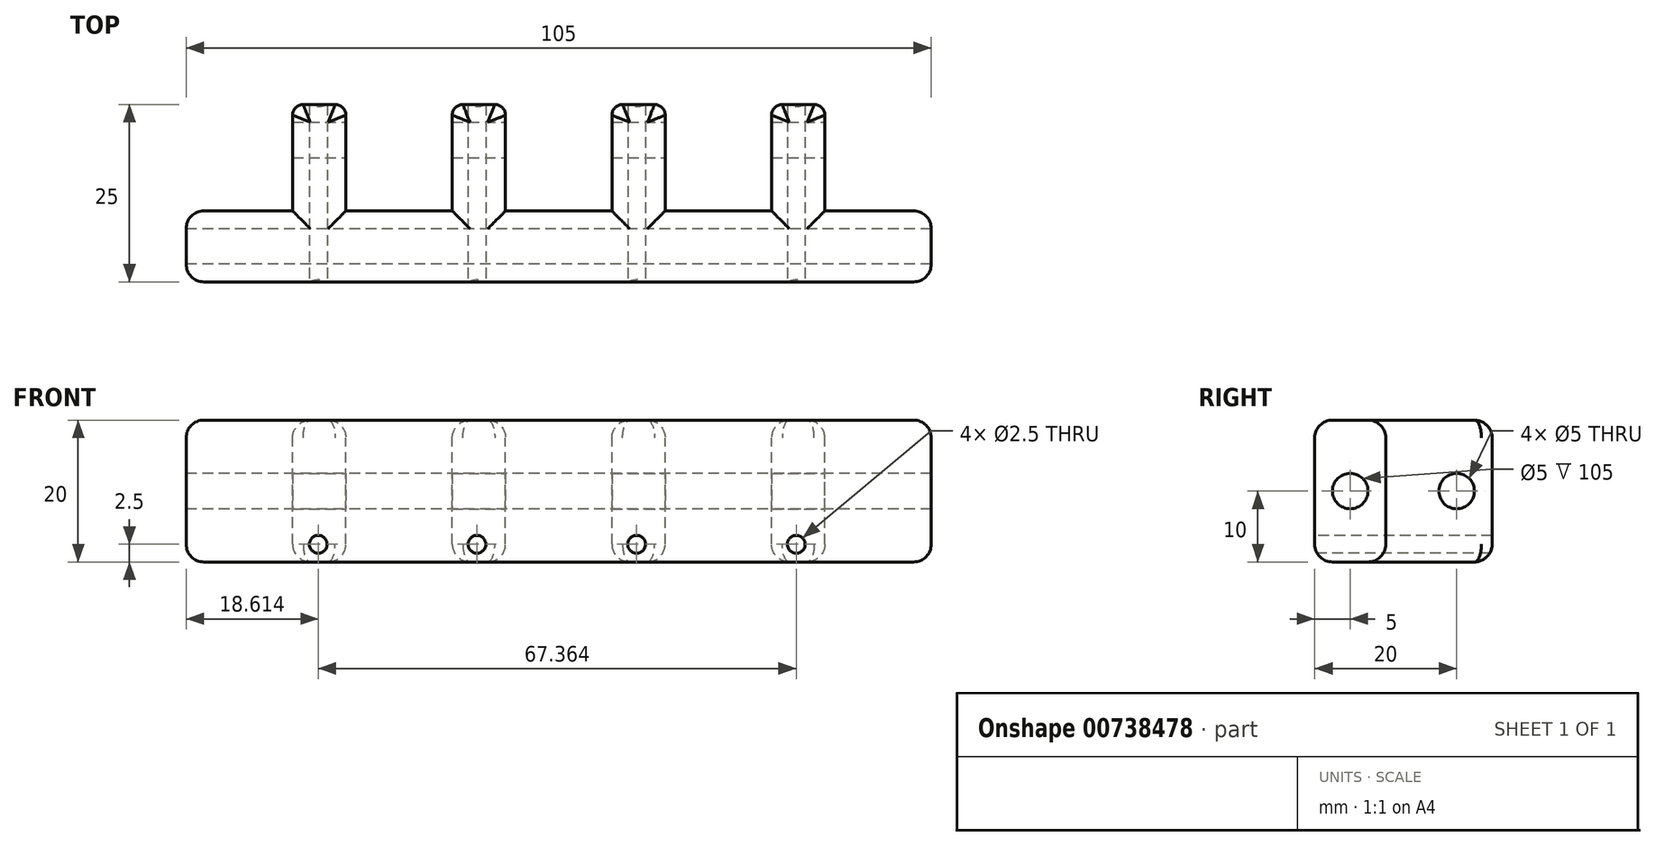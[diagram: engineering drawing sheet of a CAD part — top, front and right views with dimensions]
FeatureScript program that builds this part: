
annotation { "Feature Type Name" : "Feature", "Feature Type Description" : "" }
export const myFeature = defineFeature(function(context is Context, id is Id, definition is map)
    precondition{}
    {
        {
            var Q0;
            Q0=qCreatedBy(makeId("Top.planeOp"),FACE);
            var sketch = newSketch(context, id + "F0", { "sketchPlane" : qUnion([Q0])});
            skLineSegment(sketch, "E0.bottom", {"start": v(0, 0) * mm, "end": v(105, 0) * mm});
            skLineSegment(sketch, "E0.top", {"start": v(0, -25) * mm, "end": v(105, -25) * mm});
            skLineSegment(sketch, "E0.left", {"start": v(0, 0) * mm, "end": v(0, -25) * mm});
            skLineSegment(sketch, "E0.right", {"start": v(105, 0) * mm, "end": v(105, -25) * mm});
            skSolve(sketch);
        }
        {
            var Q0;
            Q0=makeQuery(id+"F0.imprint","IMPRINT",FACE,{"disambiguationData":[TD([[makeQuery(id+"F0.imprint","IMPRINT",EDGE,{"derivedFrom":sQuery(id+"F0.wireOp",EDGE,"E0.bottom")}),-1.0]])]});
            extrude(context, id + "F1", {"entities" : qUnion([Q0]), "depth" : 20 * mm, "offsetDistance" : 25 * mm});
        }
        {
            var Q0;
            Q0=makeQuery(id+"F1.opExtrude","CAP_FACE",FACE,{"disambiguationData":[OSD([sQuery(id+"F0.wireOp",EDGE,"E0.bottom"),sQuery(id+"F0.wireOp",EDGE,"E0.top"),sQuery(id+"F0.wireOp",EDGE,"E0.left"),sQuery(id+"F0.wireOp",EDGE,"E0.right")])],"isStart":false});
            var sketch = newSketch(context, id + "F2", { "sketchPlane" : qUnion([Q0])});
            skLineSegment(sketch, "E1", {"start": v(51.25, -10) * mm, "end": v(43.75, -10) * mm});
            skLineSegment(sketch, "E2", {"start": v(105, -15) * mm, "end": v(0, -15) * mm});
            skLineSegment(sketch, "E3", {"start": v(0, 0) * mm, "end": v(15, 0) * mm});
            skLineSegment(sketch, "E4", {"start": v(15, 0) * mm, "end": v(22.5, 0) * mm});
            skLineSegment(sketch, "E5", {"start": v(22.5, 0) * mm, "end": v(37.5, 0) * mm});
            skLineSegment(sketch, "E6", {"start": v(37.5, 0) * mm, "end": v(45, 0) * mm});
            skLineSegment(sketch, "E7", {"start": v(45, 0) * mm, "end": v(60, 0) * mm});
            skLineSegment(sketch, "E8", {"start": v(60, 0) * mm, "end": v(67.5, 0) * mm});
            skLineSegment(sketch, "E9", {"start": v(67.5, 0) * mm, "end": v(82.5, 0) * mm});
            skLineSegment(sketch, "E10", {"start": v(82.5, 0) * mm, "end": v(90, 0) * mm});
            skLineSegment(sketch, "E11", {"start": v(90, 0) * mm, "end": v(105, 0) * mm});
            skLineSegment(sketch, "E12.top", {"start": v(0, -15) * mm, "end": v(15, -15) * mm});
            skLineSegment(sketch, "E12.left", {"start": v(0, 0) * mm, "end": v(0, -15) * mm});
            skLineSegment(sketch, "E12.right", {"start": v(15, 0) * mm, "end": v(15, -15) * mm});
            skLineSegment(sketch, "E13.top", {"start": v(22.5, -15) * mm, "end": v(37.5, -15) * mm});
            skLineSegment(sketch, "E13.left", {"start": v(22.5, 0) * mm, "end": v(22.5, -15) * mm});
            skLineSegment(sketch, "E13.right", {"start": v(37.5, 0) * mm, "end": v(37.5, -15) * mm});
            skLineSegment(sketch, "E14.left", {"start": v(45, 0) * mm, "end": v(45, 0) * mm});
            skLineSegment(sketch, "E14.right", {"start": v(60, 0) * mm, "end": v(60, 0) * mm});
            skLineSegment(sketch, "E15.top", {"start": v(45, -15) * mm, "end": v(60, -15) * mm});
            skLineSegment(sketch, "E15.left", {"start": v(45, 0) * mm, "end": v(45, -15) * mm});
            skLineSegment(sketch, "E15.right", {"start": v(60, 0) * mm, "end": v(60, -15) * mm});
            skLineSegment(sketch, "E16.left", {"start": v(67.5, 0) * mm, "end": v(67.5, 0) * mm});
            skLineSegment(sketch, "E16.right", {"start": v(82.5, 0) * mm, "end": v(82.5, 0) * mm});
            skLineSegment(sketch, "E17.top", {"start": v(67.5, -15) * mm, "end": v(82.5, -15) * mm});
            skLineSegment(sketch, "E17.left", {"start": v(67.5, 0) * mm, "end": v(67.5, -15) * mm});
            skLineSegment(sketch, "E17.right", {"start": v(82.5, 0) * mm, "end": v(82.5, -15) * mm});
            skLineSegment(sketch, "E18.top", {"start": v(90, -15) * mm, "end": v(105, -15) * mm});
            skLineSegment(sketch, "E18.left", {"start": v(90, 0) * mm, "end": v(90, -15) * mm});
            skLineSegment(sketch, "E18.right", {"start": v(105, 0) * mm, "end": v(105, -15) * mm});
            skSolve(sketch);
        }
        {
            var Q0;
            Q0=makeQuery(id+"F2.imprint","IMPRINT",FACE,{"disambiguationData":[TD([[makeQuery(id+"F2.imprint","IMPRINT",EDGE,{"derivedFrom":sQuery(id+"F2.wireOp",EDGE,"E3")}),-1.0]])]});
            var Q1;
            Q1=makeQuery(id+"F2.imprint","IMPRINT",FACE,{"disambiguationData":[TD([[makeQuery(id+"F2.imprint","IMPRINT",EDGE,{"derivedFrom":sQuery(id+"F2.wireOp",EDGE,"E5")}),-1.0]])]});
            var Q2;
            Q2=makeQuery(id+"F2.imprint","IMPRINT",FACE,{"disambiguationData":[TD([[makeQuery(id+"F2.imprint","IMPRINT",EDGE,{"derivedFrom":sQuery(id+"F2.wireOp",EDGE,"E7")}),-1.0]])]});
            var Q3;
            Q3=makeQuery(id+"F2.imprint","IMPRINT",FACE,{"disambiguationData":[TD([[makeQuery(id+"F2.imprint","IMPRINT",EDGE,{"derivedFrom":sQuery(id+"F2.wireOp",EDGE,"E9")}),-1.0]])]});
            var Q4;
            Q4=makeQuery(id+"F2.imprint","IMPRINT",FACE,{"disambiguationData":[TD([[makeQuery(id+"F2.imprint","IMPRINT",EDGE,{"derivedFrom":sQuery(id+"F2.wireOp",EDGE,"E11")}),-1.0]])]});
            extrude(context, id + "F3", {"entities" : qUnion([Q0, Q1, Q2, Q3, Q4]), "operationType" : NewBodyOperationType.REMOVE, "endBound" : BoundingType.THROUGH_ALL, "oppositeDirection" : true, "depth" : 20 * mm, "offsetDistance" : 25 * mm});
        }
        {
            var Q0;
            Q0=makeQuery(id+"F3.boolean.opBoolean","COPY",FACE,{"derivedFrom":makeQuery(id+"F3.opExtrude","SWEPT_FACE",FACE,{"disambiguationData":[OSD([sQuery(id+"F2.wireOp",EDGE,"E18.left")])]})});
            var sketch = newSketch(context, id + "F4", { "sketchPlane" : qUnion([Q0])});
            skPoint(sketch, "E19.centerSnap0", {"position": v(0, 10) * mm});
            skPoint(sketch, "E19.centerSnap1", {"position": v(-7.5, 0) * mm});
            skCircle(sketch, "E20", {"center": v(-5, 10) * mm, "radius": 2.5 * mm});
            skSolve(sketch);
        }
        {
            var Q0;
            Q0=makeQuery(id+"F4.imprint","IMPRINT",FACE,{"disambiguationData":[TD([[makeQuery(id+"F4.imprint","IMPRINT",EDGE,{"derivedFrom":sQuery(id+"F4.wireOp",EDGE,"E20")}),1.0]])]});
            extrude(context, id + "F5", {"entities" : qUnion([Q0]), "operationType" : NewBodyOperationType.REMOVE, "endBound" : BoundingType.THROUGH_ALL, "oppositeDirection" : true, "depth" : 25 * mm, "offsetDistance" : 25 * mm});
        }
        {
            var Q0;
            Q0=makeQuery(id+"F1.opExtrude","SWEPT_FACE",FACE,{"disambiguationData":[OSD([sQuery(id+"F0.wireOp",EDGE,"E0.top")])]});
            var Q1;
            Q1=makeQuery(id+"F1.opExtrude","CAP_FACE",FACE,{"disambiguationData":[OSD([sQuery(id+"F0.wireOp",EDGE,"E0.bottom"),sQuery(id+"F0.wireOp",EDGE,"E0.top"),sQuery(id+"F0.wireOp",EDGE,"E0.left"),sQuery(id+"F0.wireOp",EDGE,"E0.right")])],"isStart":false});
            var Q2;
            Q2=makeQuery(id+"F1.opExtrude","SWEPT_FACE",FACE,{"disambiguationData":[OSD([sQuery(id+"F0.wireOp",EDGE,"E0.right")])]});
            var Q3;
            Q3=makeQuery(id+"F1.opExtrude","CAP_FACE",FACE,{"disambiguationData":[OSD([sQuery(id+"F0.wireOp",EDGE,"E0.bottom"),sQuery(id+"F0.wireOp",EDGE,"E0.top"),sQuery(id+"F0.wireOp",EDGE,"E0.left"),sQuery(id+"F0.wireOp",EDGE,"E0.right")])],"isStart":true});
            var Q4;
            Q4=makeQuery(id+"F1.opExtrude","SWEPT_FACE",FACE,{"disambiguationData":[OSD([sQuery(id+"F0.wireOp",EDGE,"E0.left")])]});
            fillet(context, id + "F6", {"entities" : qUnion([Q0, Q1, Q2, Q3, Q4]), "radius" : 2.5 * mm, "tangentPropagation" : true, "allowEdgeOverflow" : false});
        }
        {
            var Q0;
            {var subQ3=sQuery(id+"F0.wireOp",EDGE,"E0.bottom");Q0=makeQuery(id+"F3.boolean.opBoolean","SPLIT",FACE,{"disambiguationData":[TD([makeQuery(id+"F3.opExtrude","SWEPT_FACE",FACE,{"disambiguationData":[OSD([sQuery(id+"F2.wireOp",EDGE,"E17.right")])]})])],"derivedFrom":makeQuery(id+"F1.opExtrude","SWEPT_FACE",FACE,{"disambiguationData":[OSD([subQ3])]})});}
            var Q1;
            {var subQ3=sQuery(id+"F0.wireOp",EDGE,"E0.bottom");Q1=makeQuery(id+"F3.boolean.opBoolean","SPLIT",FACE,{"disambiguationData":[TD([makeQuery(id+"F3.opExtrude","SWEPT_FACE",FACE,{"disambiguationData":[OSD([sQuery(id+"F2.wireOp",EDGE,"E15.right")])]})])],"derivedFrom":makeQuery(id+"F1.opExtrude","SWEPT_FACE",FACE,{"disambiguationData":[OSD([subQ3])]})});}
            var Q2;
            {var subQ3=sQuery(id+"F0.wireOp",EDGE,"E0.bottom");Q2=makeQuery(id+"F3.boolean.opBoolean","SPLIT",FACE,{"disambiguationData":[TD([makeQuery(id+"F3.opExtrude","SWEPT_FACE",FACE,{"disambiguationData":[OSD([sQuery(id+"F2.wireOp",EDGE,"E13.right")])]})])],"derivedFrom":makeQuery(id+"F1.opExtrude","SWEPT_FACE",FACE,{"disambiguationData":[OSD([subQ3])]})});}
            var Q3;
            {var subQ3=sQuery(id+"F0.wireOp",EDGE,"E0.bottom");Q3=makeQuery(id+"F3.boolean.opBoolean","SPLIT",FACE,{"disambiguationData":[TD([makeQuery(id+"F3.opExtrude","SWEPT_FACE",FACE,{"disambiguationData":[OSD([sQuery(id+"F2.wireOp",EDGE,"E12.right")])]})])],"derivedFrom":makeQuery(id+"F1.opExtrude","SWEPT_FACE",FACE,{"disambiguationData":[OSD([subQ3])]})});}
            var Q4;
            Q4=makeQuery(id+"F3.boolean.opBoolean","COPY",FACE,{"derivedFrom":makeQuery(id+"F3.opExtrude","SWEPT_FACE",FACE,{"disambiguationData":[OSD([sQuery(id+"F2.wireOp",EDGE,"E18.top")])]})});
            var Q5;
            Q5=makeQuery(id+"F3.boolean.opBoolean","COPY",FACE,{"derivedFrom":makeQuery(id+"F3.opExtrude","SWEPT_FACE",FACE,{"disambiguationData":[OSD([sQuery(id+"F2.wireOp",EDGE,"E17.top")])]})});
            var Q6;
            Q6=makeQuery(id+"F3.boolean.opBoolean","COPY",FACE,{"derivedFrom":makeQuery(id+"F3.opExtrude","SWEPT_FACE",FACE,{"disambiguationData":[OSD([sQuery(id+"F2.wireOp",EDGE,"E15.top")])]})});
            var Q7;
            Q7=makeQuery(id+"F3.boolean.opBoolean","COPY",FACE,{"derivedFrom":makeQuery(id+"F3.opExtrude","SWEPT_FACE",FACE,{"disambiguationData":[OSD([sQuery(id+"F2.wireOp",EDGE,"E13.top")])]})});
            var Q8;
            Q8=makeQuery(id+"F3.boolean.opBoolean","COPY",FACE,{"derivedFrom":makeQuery(id+"F3.opExtrude","SWEPT_FACE",FACE,{"disambiguationData":[OSD([sQuery(id+"F2.wireOp",EDGE,"E12.top")])]})});
            fillet(context, id + "F7", {"entities" : qUnion([Q0, Q1, Q2, Q3, Q4, Q5, Q6, Q7, Q8]), "radius" : 1.5 * mm, "tangentPropagation" : true, "allowEdgeOverflow" : false});
        }
        {
            var Q0;
            Q0=makeQuery(id+"F1.opExtrude","SWEPT_FACE",FACE,{"disambiguationData":[OSD([sQuery(id+"F0.wireOp",EDGE,"E0.top")])]});
            var sketch = newSketch(context, id + "F8", { "sketchPlane" : qUnion([Q0])});
            skLineSegment(sketch, "E21", {"start": v(0, 0) * mm, "end": v(15, 0) * mm});
            skLineSegment(sketch, "E22", {"start": v(15, 0) * mm, "end": v(22.23, -2) * mm});
            skLineSegment(sketch, "E23", {"start": v(22.23, -2) * mm, "end": v(37.23, -2) * mm});
            skLineSegment(sketch, "E24", {"start": v(37.23, -2) * mm, "end": v(44.73, -2) * mm});
            skLineSegment(sketch, "E25", {"start": v(44.73, -2) * mm, "end": v(59.73, -2) * mm});
            skLineSegment(sketch, "E26", {"start": v(59.73, -2) * mm, "end": v(67.23, -2) * mm});
            skLineSegment(sketch, "E27", {"start": v(67.23, -2) * mm, "end": v(82.23, -2) * mm});
            skLineSegment(sketch, "E28", {"start": v(82.23, -2) * mm, "end": v(89.73, -2) * mm});
            skCircle(sketch, "E29", {"center": v(18.61, 2.5) * mm, "radius": 1.25 * mm});
            skPoint(sketch, "E29.centerSnap0", {"position": v(18.61, -1) * mm});
            skCircle(sketch, "E30", {"center": v(40.98, 2.5) * mm, "radius": 1.25 * mm});
            skPoint(sketch, "E30.centerSnap0", {"position": v(40.98, -2) * mm});
            skCircle(sketch, "E31", {"center": v(63.48, 2.5) * mm, "radius": 1.25 * mm});
            skPoint(sketch, "E31.centerSnap0", {"position": v(63.48, -2) * mm});
            skCircle(sketch, "E32", {"center": v(85.98, 2.5) * mm, "radius": 1.25 * mm});
            skPoint(sketch, "E32.centerSnap0", {"position": v(85.98, -2) * mm});
            skSolve(sketch);
        }
        {
            var Q0;
            {var subQ0=sQuery(id+"F8.wireOp",EDGE,"E29");var subQ1=sQuery(id+"F0.wireOp",EDGE,"E0.top");var subQ2=makeQuery(id+"F6.opFillet","BLEND_EDGE",EDGE,{"blendedFrom":[makeQuery(id+"F1.opExtrude","CAP_EDGE",EDGE,{"disambiguationData":[OSD([subQ1])],"isStart":true}),makeQuery(id+"F1.opExtrude","SWEPT_FACE",FACE,{"disambiguationData":[OSD([subQ1])]})],"blendedInto":[makeQuery(id+"F1.opExtrude","SWEPT_FACE",FACE,{"disambiguationData":[OSD([subQ1])]})]});var subQ3=makeQuery(id+"F8.imprint","INTERSECT",VERTEX,{"disambiguationData":[OD(0.0)],"derivedFrom":[subQ2,subQ0]});Q0=makeQuery(id+"F8.imprint","IMPRINT",FACE,{"disambiguationData":[TD([[makeQuery(id+"F8.imprint","IMPRINT",EDGE,{"disambiguationData":[TD([[subQ3,-1.0]])],"derivedFrom":subQ0}),1.0]])]});}
            var Q1;
            {var subQ0=sQuery(id+"F8.wireOp",EDGE,"E29");var subQ1=sQuery(id+"F0.wireOp",EDGE,"E0.top");var subQ2=makeQuery(id+"F6.opFillet","BLEND_EDGE",EDGE,{"blendedFrom":[makeQuery(id+"F1.opExtrude","CAP_EDGE",EDGE,{"disambiguationData":[OSD([subQ1])],"isStart":true}),makeQuery(id+"F1.opExtrude","SWEPT_FACE",FACE,{"disambiguationData":[OSD([subQ1])]})],"blendedInto":[makeQuery(id+"F1.opExtrude","SWEPT_FACE",FACE,{"disambiguationData":[OSD([subQ1])]})]});var subQ3=makeQuery(id+"F8.imprint","INTERSECT",VERTEX,{"disambiguationData":[OD(0.0)],"derivedFrom":[subQ2,subQ0]});Q1=makeQuery(id+"F8.imprint","IMPRINT",FACE,{"disambiguationData":[TD([[makeQuery(id+"F8.imprint","IMPRINT",EDGE,{"disambiguationData":[TD([[subQ3,1.0]])],"derivedFrom":subQ0}),1.0]])]});}
            var Q2;
            {var subQ0=sQuery(id+"F8.wireOp",EDGE,"E30");var subQ1=sQuery(id+"F0.wireOp",EDGE,"E0.top");var subQ2=makeQuery(id+"F6.opFillet","BLEND_EDGE",EDGE,{"blendedFrom":[makeQuery(id+"F1.opExtrude","CAP_EDGE",EDGE,{"disambiguationData":[OSD([subQ1])],"isStart":true}),makeQuery(id+"F1.opExtrude","SWEPT_FACE",FACE,{"disambiguationData":[OSD([subQ1])]})],"blendedInto":[makeQuery(id+"F1.opExtrude","SWEPT_FACE",FACE,{"disambiguationData":[OSD([subQ1])]})]});var subQ3=makeQuery(id+"F8.imprint","INTERSECT",VERTEX,{"disambiguationData":[OD(0.0)],"derivedFrom":[subQ2,subQ0]});Q2=makeQuery(id+"F8.imprint","IMPRINT",FACE,{"disambiguationData":[TD([[makeQuery(id+"F8.imprint","IMPRINT",EDGE,{"disambiguationData":[TD([[subQ3,1.0]])],"derivedFrom":subQ0}),1.0]])]});}
            var Q3;
            {var subQ0=sQuery(id+"F8.wireOp",EDGE,"E30");var subQ1=sQuery(id+"F0.wireOp",EDGE,"E0.top");var subQ2=makeQuery(id+"F6.opFillet","BLEND_EDGE",EDGE,{"blendedFrom":[makeQuery(id+"F1.opExtrude","CAP_EDGE",EDGE,{"disambiguationData":[OSD([subQ1])],"isStart":true}),makeQuery(id+"F1.opExtrude","SWEPT_FACE",FACE,{"disambiguationData":[OSD([subQ1])]})],"blendedInto":[makeQuery(id+"F1.opExtrude","SWEPT_FACE",FACE,{"disambiguationData":[OSD([subQ1])]})]});var subQ3=makeQuery(id+"F8.imprint","INTERSECT",VERTEX,{"disambiguationData":[OD(0.0)],"derivedFrom":[subQ2,subQ0]});Q3=makeQuery(id+"F8.imprint","IMPRINT",FACE,{"disambiguationData":[TD([[makeQuery(id+"F8.imprint","IMPRINT",EDGE,{"disambiguationData":[TD([[subQ3,-1.0]])],"derivedFrom":subQ0}),1.0]])]});}
            var Q4;
            {var subQ0=sQuery(id+"F8.wireOp",EDGE,"E31");var subQ1=sQuery(id+"F0.wireOp",EDGE,"E0.top");var subQ2=makeQuery(id+"F6.opFillet","BLEND_EDGE",EDGE,{"blendedFrom":[makeQuery(id+"F1.opExtrude","CAP_EDGE",EDGE,{"disambiguationData":[OSD([subQ1])],"isStart":true}),makeQuery(id+"F1.opExtrude","SWEPT_FACE",FACE,{"disambiguationData":[OSD([subQ1])]})],"blendedInto":[makeQuery(id+"F1.opExtrude","SWEPT_FACE",FACE,{"disambiguationData":[OSD([subQ1])]})]});var subQ3=makeQuery(id+"F8.imprint","INTERSECT",VERTEX,{"disambiguationData":[OD(0.0)],"derivedFrom":[subQ2,subQ0]});Q4=makeQuery(id+"F8.imprint","IMPRINT",FACE,{"disambiguationData":[TD([[makeQuery(id+"F8.imprint","IMPRINT",EDGE,{"disambiguationData":[TD([[subQ3,-1.0]])],"derivedFrom":subQ0}),1.0]])]});}
            var Q5;
            {var subQ0=sQuery(id+"F8.wireOp",EDGE,"E31");var subQ1=sQuery(id+"F0.wireOp",EDGE,"E0.top");var subQ2=makeQuery(id+"F6.opFillet","BLEND_EDGE",EDGE,{"blendedFrom":[makeQuery(id+"F1.opExtrude","CAP_EDGE",EDGE,{"disambiguationData":[OSD([subQ1])],"isStart":true}),makeQuery(id+"F1.opExtrude","SWEPT_FACE",FACE,{"disambiguationData":[OSD([subQ1])]})],"blendedInto":[makeQuery(id+"F1.opExtrude","SWEPT_FACE",FACE,{"disambiguationData":[OSD([subQ1])]})]});var subQ3=makeQuery(id+"F8.imprint","INTERSECT",VERTEX,{"disambiguationData":[OD(0.0)],"derivedFrom":[subQ2,subQ0]});Q5=makeQuery(id+"F8.imprint","IMPRINT",FACE,{"disambiguationData":[TD([[makeQuery(id+"F8.imprint","IMPRINT",EDGE,{"disambiguationData":[TD([[subQ3,1.0]])],"derivedFrom":subQ0}),1.0]])]});}
            var Q6;
            {var subQ0=sQuery(id+"F8.wireOp",EDGE,"E32");var subQ1=sQuery(id+"F0.wireOp",EDGE,"E0.top");var subQ2=makeQuery(id+"F6.opFillet","BLEND_EDGE",EDGE,{"blendedFrom":[makeQuery(id+"F1.opExtrude","CAP_EDGE",EDGE,{"disambiguationData":[OSD([subQ1])],"isStart":true}),makeQuery(id+"F1.opExtrude","SWEPT_FACE",FACE,{"disambiguationData":[OSD([subQ1])]})],"blendedInto":[makeQuery(id+"F1.opExtrude","SWEPT_FACE",FACE,{"disambiguationData":[OSD([subQ1])]})]});var subQ3=makeQuery(id+"F8.imprint","INTERSECT",VERTEX,{"disambiguationData":[OD(0.0)],"derivedFrom":[subQ2,subQ0]});Q6=makeQuery(id+"F8.imprint","IMPRINT",FACE,{"disambiguationData":[TD([[makeQuery(id+"F8.imprint","IMPRINT",EDGE,{"disambiguationData":[TD([[subQ3,1.0]])],"derivedFrom":subQ0}),1.0]])]});}
            var Q7;
            {var subQ0=sQuery(id+"F8.wireOp",EDGE,"E32");var subQ1=sQuery(id+"F0.wireOp",EDGE,"E0.top");var subQ2=makeQuery(id+"F6.opFillet","BLEND_EDGE",EDGE,{"blendedFrom":[makeQuery(id+"F1.opExtrude","CAP_EDGE",EDGE,{"disambiguationData":[OSD([subQ1])],"isStart":true}),makeQuery(id+"F1.opExtrude","SWEPT_FACE",FACE,{"disambiguationData":[OSD([subQ1])]})],"blendedInto":[makeQuery(id+"F1.opExtrude","SWEPT_FACE",FACE,{"disambiguationData":[OSD([subQ1])]})]});var subQ3=makeQuery(id+"F8.imprint","INTERSECT",VERTEX,{"disambiguationData":[OD(0.0)],"derivedFrom":[subQ2,subQ0]});Q7=makeQuery(id+"F8.imprint","IMPRINT",FACE,{"disambiguationData":[TD([[makeQuery(id+"F8.imprint","IMPRINT",EDGE,{"disambiguationData":[TD([[subQ3,-1.0]])],"derivedFrom":subQ0}),1.0]])]});}
            extrude(context, id + "F9", {"entities" : qUnion([Q0, Q1, Q2, Q3, Q4, Q5, Q6, Q7]), "operationType" : NewBodyOperationType.REMOVE, "endBound" : BoundingType.THROUGH_ALL, "oppositeDirection" : true, "depth" : 25 * mm, "offsetDistance" : 25 * mm});
        }
        {
            var Q0;
            Q0=makeQuery(id+"F1.opExtrude","SWEPT_FACE",FACE,{"disambiguationData":[OSD([sQuery(id+"F0.wireOp",EDGE,"E0.left")])]});
            var sketch = newSketch(context, id + "F10", { "sketchPlane" : qUnion([Q0])});
            skCircle(sketch, "E33", {"center": v(20, 10) * mm, "radius": 2.5 * mm});
            skPoint(sketch, "E33.centerSnap0", {"position": v(17.5, 10) * mm});
            skPoint(sketch, "E33.centerSnap1", {"position": v(20, 2.5) * mm});
            skSolve(sketch);
        }
        {
            var Q0;
            Q0=makeQuery(id+"F10.imprint","IMPRINT",FACE,{"disambiguationData":[TD([[makeQuery(id+"F10.imprint","IMPRINT",EDGE,{"derivedFrom":sQuery(id+"F10.wireOp",EDGE,"E33")}),1.0]])]});
            extrude(context, id + "F11", {"entities" : qUnion([Q0]), "operationType" : NewBodyOperationType.REMOVE, "endBound" : BoundingType.THROUGH_ALL, "oppositeDirection" : true, "depth" : 25 * mm, "offsetDistance" : 25 * mm});
        }
    });
